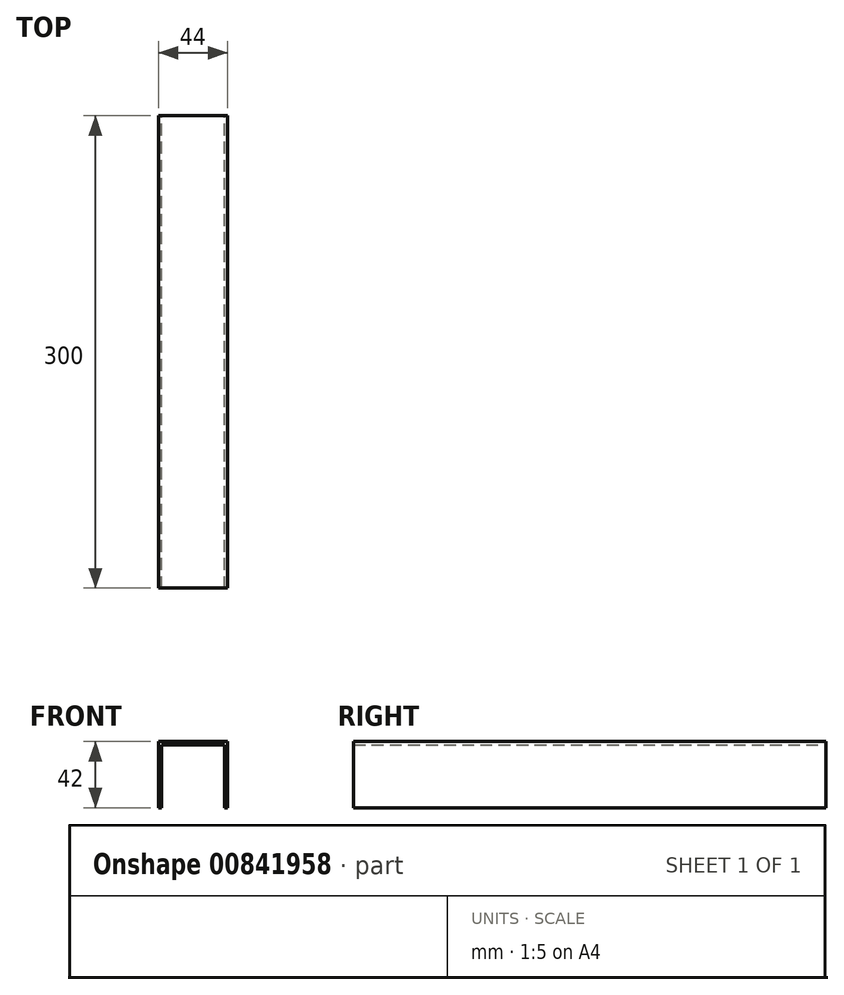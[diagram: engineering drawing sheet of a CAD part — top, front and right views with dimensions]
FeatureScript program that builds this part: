
annotation { "Feature Type Name" : "Feature", "Feature Type Description" : "" }
export const myFeature = defineFeature(function(context is Context, id is Id, definition is map)
    precondition{}
    {
        {
            var Q0;
            Q0=qCreatedBy(makeId("Front.planeOp"),FACE);
            var sketch = newSketch(context, id + "F0", { "sketchPlane" : qUnion([Q0])});
            skLineSegment(sketch, "E0", {"start": v(-20, 0) * mm, "end": v(-20, 40) * mm});
            skLineSegment(sketch, "E1", {"start": v(-20, 40) * mm, "end": v(20, 40) * mm});
            skLineSegment(sketch, "E2", {"start": v(20, 40) * mm, "end": v(20, 0) * mm});
            skLineSegment(sketch, "E3.0", {"start": v(22, 42) * mm, "end": v(22, 0) * mm});
            skLineSegment(sketch, "E3.1", {"start": v(-22, 42) * mm, "end": v(22, 42) * mm});
            skLineSegment(sketch, "E3.2", {"start": v(-22, 0) * mm, "end": v(-22, 42) * mm});
            skLineSegment(sketch, "E4", {"start": v(-22, 0) * mm, "end": v(-20, 0) * mm});
            skLineSegment(sketch, "E5", {"start": v(20, 0) * mm, "end": v(22, 0) * mm});
            skSolve(sketch);
        }
        {
            var Q0;
            Q0=makeQuery(id+"F0.imprint","IMPRINT",FACE,{"disambiguationData":[TD([[makeQuery(id+"F0.imprint","IMPRINT",EDGE,{"derivedFrom":sQuery(id+"F0.wireOp",EDGE,"E0")}),1.0]])]});
            extrude(context, id + "F1", {"entities" : qUnion([Q0]), "endBound" : BoundingType.SYMMETRIC, "depth" : 300 * mm, "offsetDistance" : 25 * mm});
        }
    });
